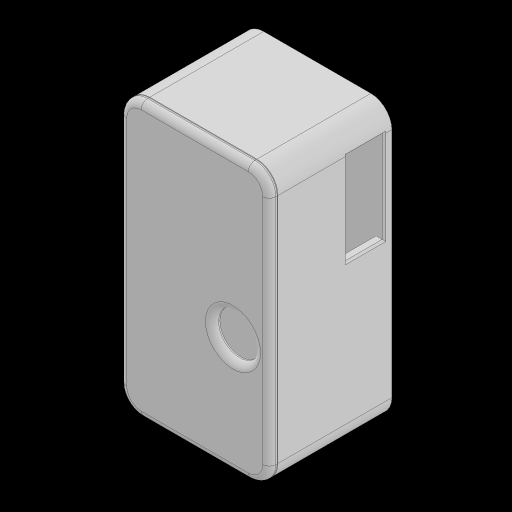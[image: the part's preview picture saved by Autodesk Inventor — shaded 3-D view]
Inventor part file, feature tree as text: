
AUTODESK INVENTOR PART (.ipt)
format: ipt  version: 2024 (Build 280153000, 153)  size: 871,424 bytes
history: native  units: mm
features: sketch x34, extrude x33, projected_geometry x20, other x3, fillet x3, chamfer x3, hole x1, plane x1
ambient origin geometry x8: Origin, YZ Plane, XZ Plane, XY Plane, X Axis, Y Axis, Z Axis, Center Point
bodies: Body1 (feature_tree), Body2 (feature_tree), Body3 (feature_tree)
feature tree (98):
  other  "Main Board"
  extrude  "Extrusion1"  Depth=50.81mm
  hole  "Hole1"  [1 undecoded]
  extrude  "Extrusion2"  Depth=8.0mm
  extrude  "Extrusion3"  Depth=1.65mm
  extrude  "Extrusion4"  Depth=6.6mm
  extrude  "Extrusion5"  Depth=4.2mm
  extrude  "Extrusion6"  Depth=4.2mm
  extrude  "Extrusion7"  Depth=4.6mm TaperAngle=0.0deg
  extrude  "Extrusion8"  Depth=6.0mm
  extrude  "Extrusion9"  Depth=1.7mm
  extrude  "Extrusion10"  Depth=5.6mm TaperAngle=0.0deg
  extrude  "Extrusion11"  Depth=1.6mm TaperAngle=0.0deg
  extrude  "Extrusion12"  Depth=39.3mm
  extrude  "Extrusion13"  Depth=2.86mm
  extrude  "Extrusion14"  Depth=6.0mm TaperAngle=0.0deg
  extrude  "Extrusion15"  Depth=39.3mm
  extrude  "Extrusion16"  Depth=1.435mm
  extrude  "Extrusion17"  Depth=9.2mm
  extrude  "Extrusion18"  Depth=9.2mm
  extrude  "Extrusion19"  Depth=36.43mm
  extrude  "Extrusion20"  Depth=8.0mm
  extrude  "Extrusion21"  Depth=15.91mm
  extrude  "Extrusion22"  Depth=0.08mm
  extrude  "Extrusion23"  Depth=15.91mm
  sketch  "Sketch26"  dims[d67=14.0mm d68=0.0mm d69=0.6mm]
  sketch  "Sketch27"  dims[d70=10.0mm d71=7.82mm d72=12.09mm]
  plane  "Work Plane1"
  extrude  "Extrusion26"  Depth=0.6mm
  extrude  "Extrusion27"  Depth=10.0mm
  fillet  "Fillet2"  Radius=12.09mm
  extrude  "Extrusion29"  Depth=3.73mm
  fillet  "Fillet3"  Radius=3.635mm
  extrude  "Extrusion30"  Depth=16.11mm
  extrude  "Extrusion31"  Depth=3.635mm TaperAngle=0.0deg
  fillet  "Fillet5"  Radius=0.1mm
  extrude  "Extrusion35"  Depth=57.37mm
  chamfer  "Chamfer5"  Distance=2.34mm
  extrude  "Extrusion36"  Depth=1.0mm TaperAngle=0.0deg
  extrude  "Extrusion37"  Depth=18.0mm
  extrude  "Extrusion38"  Depth=24.5mm
  chamfer  "Chamfer6"  Distance=6.3mm
  extrude  "Extrusion39"  Depth=0.7mm TaperAngle=0.0deg
  chamfer  "Chamfer7"  Distance=4.0mm
  sketch  "Sketch1"  dims[d0=98.33mm d1=50.81mm]
  sketch  "Sketch2"  dims[d2=5.0mm d3=1.54mm d4=0.0mm]
  sketch  "Sketch3"  dims[d5=4.0mm d6=6.0mm d7=4.0mm d8=2.0mm d9=90.0deg d10=8.0mm d11=20.594885mm d12=21.45mm]
  sketch  "Sketch4"  dims[d13=20.1mm d14=1.65mm]
  sketch  "Sketch5"  dims[d15=4.53mm d16=6.6mm]
  sketch  "Sketch6"  dims[d17=4.0mm d18=4.2mm]
  sketch  "Sketch7"  dims[d19=4.0mm d20=4.2mm]
  sketch  "Sketch9"  dims[d22=2.0mm d23=4.6mm d24=0.0mm]
  sketch  "Sketch10"  dims[d25=1.2mm d26=0.0mm d27=6.0mm]
  sketch  "Sketch11"  dims[d28=6.0mm d29=1.7mm]
  sketch  "Sketch12"  dims[d30=15.3mm d31=5.6mm d32=0.0mm]
  sketch  "Sketch13"  dims[d33=3.44mm d34=1.6mm d35=0.0mm]
  projected_geometry  "Projected Loop1"
  projected_geometry  "Projected Loop2"
  sketch  "Sketch14"  dims[d36=17.6mm d37=39.3mm]
  sketch  "Sketch15"  dims[d38=36.46mm d39=2.86mm]
  sketch  "Sketch16"  dims[d40=1.42mm d41=6.0mm d42=0.0mm]
  sketch  "Sketch17"  dims[d43=36.43mm d44=39.3mm]
  sketch  "Sketch18"  dims[d45=1.435mm d46=2.84mm]
  sketch  "Sketch19"  dims[d47=8.4mm d48=0.0mm d49=9.2mm]
  projected_geometry  "Projected Loop3"
  sketch  "Sketch20"  dims[d50=9.2mm d51=9.2mm]
  sketch  "Sketch21"  dims[d53=27.6mm d54=36.43mm]
  sketch  "Sketch22"  dims[d56=4.415mm d57=8.0mm]
  sketch  "Sketch23"  dims[d58=3.75mm d59=0.0mm d60=15.91mm]
  projected_geometry  "Projected Loop4"
  other  "Case"
  sketch  "Sketch24"  dims[d61=16.11mm d62=0.08mm]
  projected_geometry  "Projected Loop5"
  sketch  "Sketch25"  dims[d63=27.55mm d64=15.91mm d65=16.11mm d66=3.71mm]
  projected_geometry  "Projected Loop6"
  projected_geometry  "Projected Loop7"
  projected_geometry  "Projected Loop8"
  projected_geometry  "Projected Loop9"
  projected_geometry  "Projected Loop10"
  projected_geometry  "Projected Loop11"
  projected_geometry  "Projected Loop12"
  sketch  "Sketch28"  dims[d73=4.82mm d74=3.73mm d75=3.635mm]
  projected_geometry  "Projected Loop13"
  other  "Lid"
  sketch  "Sketch29"  dims[d76=2.01mm d77=16.11mm]
  projected_geometry  "Projected Loop14"
  sketch  "Sketch32"  dims[d78=0.05mm]
  projected_geometry  "Projected Loop15"
  projected_geometry  "Projected Loop16"
  sketch  "Sketch34"  dims[d79=7.82mm d80=12.09mm d81=4.82mm d82=3.73mm d83=3.635mm d84=14.9mm d85=0.0mm d86=0.1mm d87=0.0mm]
  projected_geometry  "Projected Loop18"
  sketch  "Sketch35"  dims[d88=2.34mm d89=57.37mm]
  projected_geometry  "Projected Loop19"
  sketch  "Sketch39"  dims[d90=66.48mm]
  projected_geometry  "Projected Loop23"
  sketch  "Sketch40"  dims[d91=3.25mm d92=2.34mm d93=57.37mm d94=22.97mm]
  sketch  "Sketch41"  dims[d95=11.8mm d96=0.0mm d97=1.0mm d98=0.0mm d99=18.0mm d100=24.5mm d101=6.3mm d102=0.7mm d103=0.0mm d104=4.0mm d105=3.0mm d106=6.55mm d107=31.41mm d108=1.9mm d109=0.0mm d110=3.0mm d111=12.8mm d112=35.0mm d113=4.0mm d114=1.9mm d115=0.0mm d116=2.3mm d117=2.3mm d118=0.5mm d119=0.0mm d120=9.0mm d121=3.3mm d122=1.5mm d123=3.7mm d124=9.0mm d125=3.3mm d126=1.5mm d127=2.9mm d128=0.3mm d129=0.3mm d130=7.4mm d131=0.0mm d132=50.0mm d134=2.54mm d135=20.0mm d137=2.54mm d140=2.3mm d141=11.7mm d142=7.4mm d143=0.0mm d144=2.42mm d145=0.0mm d147=1.0mm d148=2.0mm d149=2.0mm d150=0.0mm d151=2.0mm d152=24.36mm d153=0.0mm d154=1.0mm d155=4.0mm d156=0.0mm d157=1.0mm d158=1.0mm d162=7.0mm d163=7.0mm d164=7.0mm d165=7.0mm d174=0.3mm d175=0.8mm d176=10.0mm d177=0.0mm d178=3.0mm d179=0.0mm d180=2.5mm d181=3.5mm d182=3.5mm d190=16.0mm d191=10.0mm d192=0.0mm d193=2.5mm d196=3.0mm d197=14.0mm d198=0.0mm d199=3.0mm d200=0.0mm d201=2.5mm d216=14.0mm d217=35.0mm d218=10.0mm d219=0.0mm d220=0.7mm d221=2.0mm d222=45.0deg d223=45.0deg d224=10.0mm d225=0.0mm d226=10.0mm d227=0.0mm d229=2.0mm d230=2.0mm d231=10.0mm d232=0.0mm d233=0.7mm d234=2.0mm d235=45.0deg d236=1.0mm d237=1.0mm d238=1.0mm d239=1.0mm d240=4.0mm d241=0.0mm d242=0.7mm d243=2.0mm d244=45.0deg d185=0.5mm d186=0.872665mm d187=0.5mm d188=0.872665mm d204=0.5mm d205=0.872665mm d206=0.5mm d207=0.872665mm d208=0.5mm d209=0.872665mm]
  projected_geometry  "Projected Loop24"
note: 1 required parameter value undecoded (feature->parameter linkage not recoverable at this tier; creation-order binding heuristic only, values carry confidence <= 0.55)
